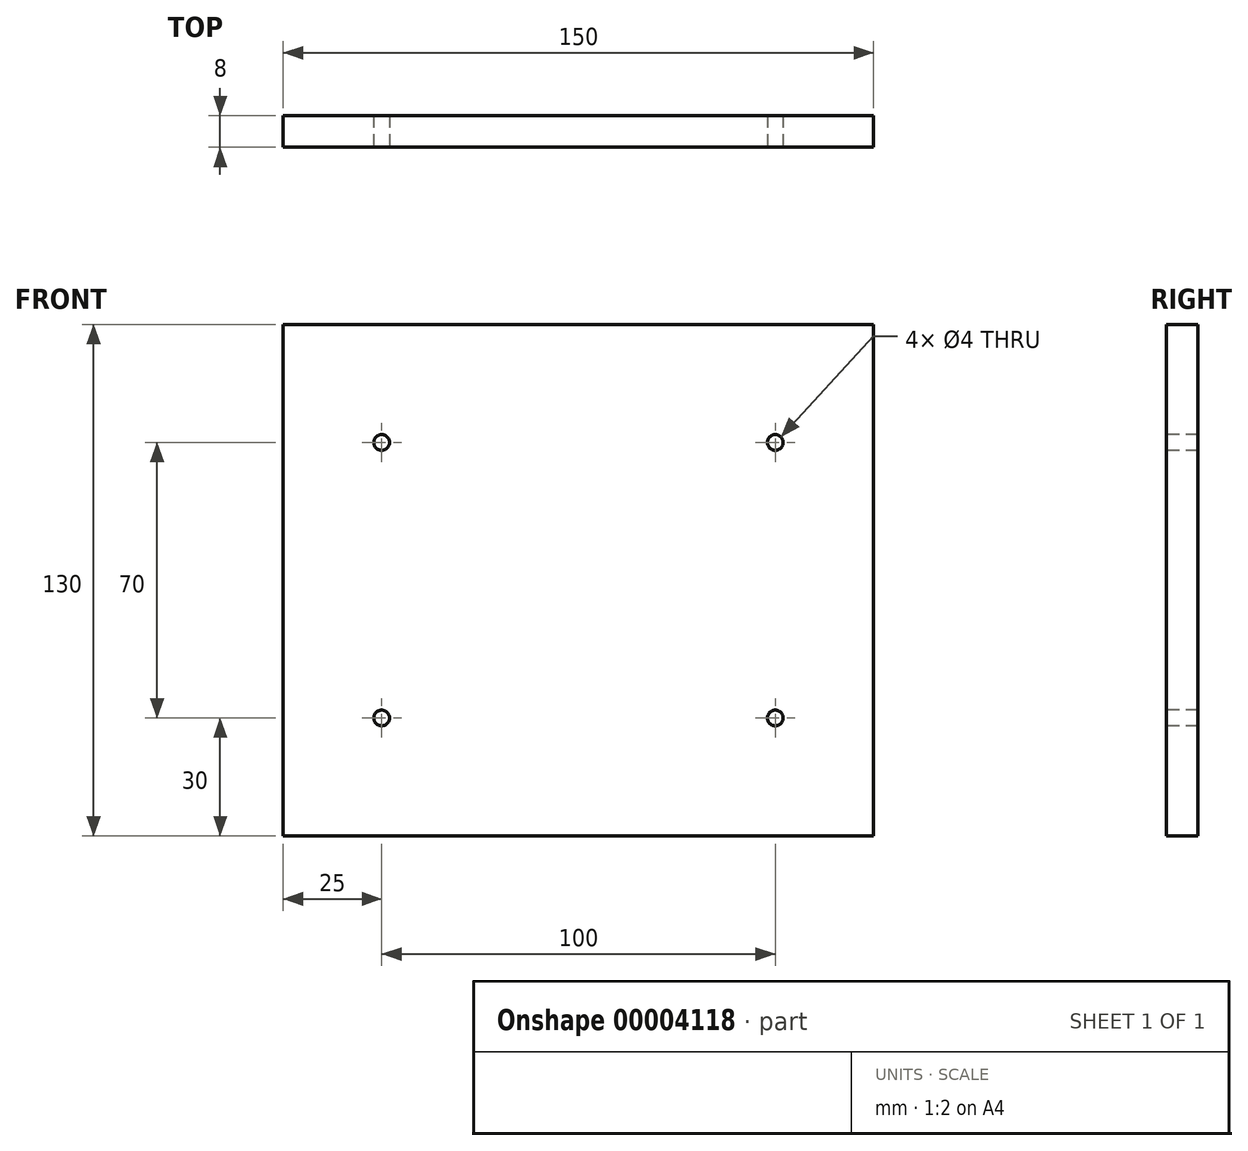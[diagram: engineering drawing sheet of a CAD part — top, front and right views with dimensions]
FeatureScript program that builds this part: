
annotation { "Feature Type Name" : "Feature", "Feature Type Description" : "" }
export const myFeature = defineFeature(function(context is Context, id is Id, definition is map)
    precondition{}
    {
        {
            var Q0;
            Q0=qCreatedBy(makeId("Front.planeOp"),FACE);
            var sketch = newSketch(context, id + "F0", { "sketchPlane" : qUnion([Q0])});
            skLineSegment(sketch, "E0.bottom", {"start": v(-150, 130) * mm, "end": v(0, 130) * mm});
            skLineSegment(sketch, "E0.top", {"start": v(-150, 0) * mm, "end": v(0, 0) * mm});
            skLineSegment(sketch, "E0.left", {"start": v(-150, 130) * mm, "end": v(-150, 0) * mm});
            skLineSegment(sketch, "E0.right", {"start": v(0, 130) * mm, "end": v(0, 0) * mm});
            skSolve(sketch);
        }
        {
            var Q0;
            Q0=makeQuery(id+"F0.imprint","IMPRINT",FACE,{"disambiguationData":[TD([[makeQuery(id+"F0.imprint","IMPRINT",EDGE,{"derivedFrom":sQuery(id+"F0.wireOp",EDGE,"E0.bottom")}),-1.0]])]});
            extrude(context, id + "F1", {"entities" : qUnion([Q0]), "depth" : 8 * mm});
        }
        {
            var Q0;
            Q0=makeQuery(id+"F1.opExtrude","CAP_FACE",FACE,{"disambiguationData":[OSD([sQuery(id+"F0.wireOp",EDGE,"E0.bottom"),sQuery(id+"F0.wireOp",EDGE,"E0.top"),sQuery(id+"F0.wireOp",EDGE,"E0.left"),sQuery(id+"F0.wireOp",EDGE,"E0.right")])],"isStart":false});
            var sketch = newSketch(context, id + "F2", { "sketchPlane" : qUnion([Q0])});
            skLineSegment(sketch, "E1", {"start": v(-75, 130) * mm, "end": v(-75, 0) * mm});
            skLineSegment(sketch, "E2", {"start": v(-150, 100) * mm, "end": v(0, 100) * mm});
            skLineSegment(sketch, "E3", {"start": v(-150, 30) * mm, "end": v(0, 30) * mm});
            skCircle(sketch, "E4", {"center": v(-125, 100) * mm, "radius": 2 * mm});
            skCircle(sketch, "E5", {"center": v(-25, 100) * mm, "radius": 2 * mm});
            skCircle(sketch, "E6", {"center": v(-125, 30) * mm, "radius": 2 * mm});
            skCircle(sketch, "E7", {"center": v(-25, 30) * mm, "radius": 2 * mm});
            skSolve(sketch);
        }
        {
            var Q0;
            {var subQ0=sQuery(id+"F2.wireOp",EDGE,"E4");var subQ1=sQuery(id+"F2.wireOp",EDGE,"E2");var subQ3=makeQuery(id+"F2.imprint","INTERSECT",VERTEX,{"disambiguationData":[OD(0.0)],"derivedFrom":[subQ1,subQ0]});Q0=makeQuery(id+"F2.imprint","IMPRINT",FACE,{"disambiguationData":[TD([[makeQuery(id+"F2.imprint","IMPRINT",EDGE,{"disambiguationData":[TD([[subQ3,-1.0]])],"derivedFrom":subQ1}),-1.0]])]});}
            var Q1;
            {var subQ0=sQuery(id+"F2.wireOp",EDGE,"E4");var subQ1=sQuery(id+"F2.wireOp",EDGE,"E2");var subQ3=makeQuery(id+"F2.imprint","INTERSECT",VERTEX,{"disambiguationData":[OD(0.0)],"derivedFrom":[subQ1,subQ0]});Q1=makeQuery(id+"F2.imprint","IMPRINT",FACE,{"disambiguationData":[TD([[makeQuery(id+"F2.imprint","IMPRINT",EDGE,{"disambiguationData":[TD([[subQ3,-1.0]])],"derivedFrom":subQ1}),1.0]])]});}
            var Q2;
            {var subQ0=sQuery(id+"F2.wireOp",EDGE,"E5");var subQ1=sQuery(id+"F2.wireOp",EDGE,"E2");var subQ3=makeQuery(id+"F2.imprint","INTERSECT",VERTEX,{"disambiguationData":[OD(0.0)],"derivedFrom":[subQ1,subQ0]});Q2=makeQuery(id+"F2.imprint","IMPRINT",FACE,{"disambiguationData":[TD([[makeQuery(id+"F2.imprint","IMPRINT",EDGE,{"disambiguationData":[TD([[subQ3,-1.0]])],"derivedFrom":subQ1}),-1.0]])]});}
            var Q3;
            {var subQ0=sQuery(id+"F2.wireOp",EDGE,"E5");var subQ1=sQuery(id+"F2.wireOp",EDGE,"E2");var subQ3=makeQuery(id+"F2.imprint","INTERSECT",VERTEX,{"disambiguationData":[OD(0.0)],"derivedFrom":[subQ1,subQ0]});Q3=makeQuery(id+"F2.imprint","IMPRINT",FACE,{"disambiguationData":[TD([[makeQuery(id+"F2.imprint","IMPRINT",EDGE,{"disambiguationData":[TD([[subQ3,-1.0]])],"derivedFrom":subQ1}),1.0]])]});}
            var Q4;
            {var subQ0=sQuery(id+"F2.wireOp",EDGE,"E6");var subQ1=sQuery(id+"F2.wireOp",EDGE,"E3");var subQ3=makeQuery(id+"F2.imprint","INTERSECT",VERTEX,{"disambiguationData":[OD(0.0)],"derivedFrom":[subQ1,subQ0]});Q4=makeQuery(id+"F2.imprint","IMPRINT",FACE,{"disambiguationData":[TD([[makeQuery(id+"F2.imprint","IMPRINT",EDGE,{"disambiguationData":[TD([[subQ3,-1.0]])],"derivedFrom":subQ1}),1.0]])]});}
            var Q5;
            {var subQ0=sQuery(id+"F2.wireOp",EDGE,"E6");var subQ1=sQuery(id+"F2.wireOp",EDGE,"E3");var subQ3=makeQuery(id+"F2.imprint","INTERSECT",VERTEX,{"disambiguationData":[OD(0.0)],"derivedFrom":[subQ1,subQ0]});Q5=makeQuery(id+"F2.imprint","IMPRINT",FACE,{"disambiguationData":[TD([[makeQuery(id+"F2.imprint","IMPRINT",EDGE,{"disambiguationData":[TD([[subQ3,-1.0]])],"derivedFrom":subQ1}),-1.0]])]});}
            var Q6;
            {var subQ0=sQuery(id+"F2.wireOp",EDGE,"E7");var subQ1=sQuery(id+"F2.wireOp",EDGE,"E3");var subQ3=makeQuery(id+"F2.imprint","INTERSECT",VERTEX,{"disambiguationData":[OD(0.0)],"derivedFrom":[subQ1,subQ0]});Q6=makeQuery(id+"F2.imprint","IMPRINT",FACE,{"disambiguationData":[TD([[makeQuery(id+"F2.imprint","IMPRINT",EDGE,{"disambiguationData":[TD([[subQ3,-1.0]])],"derivedFrom":subQ1}),1.0]])]});}
            var Q7;
            {var subQ0=sQuery(id+"F2.wireOp",EDGE,"E7");var subQ1=sQuery(id+"F2.wireOp",EDGE,"E3");var subQ3=makeQuery(id+"F2.imprint","INTERSECT",VERTEX,{"disambiguationData":[OD(0.0)],"derivedFrom":[subQ1,subQ0]});Q7=makeQuery(id+"F2.imprint","IMPRINT",FACE,{"disambiguationData":[TD([[makeQuery(id+"F2.imprint","IMPRINT",EDGE,{"disambiguationData":[TD([[subQ3,-1.0]])],"derivedFrom":subQ1}),-1.0]])]});}
            extrude(context, id + "F3", {"entities" : qUnion([Q0, Q1, Q2, Q3, Q4, Q5, Q6, Q7]), "operationType" : NewBodyOperationType.REMOVE, "oppositeDirection" : true, "depth" : 25 * mm});
        }
    });
